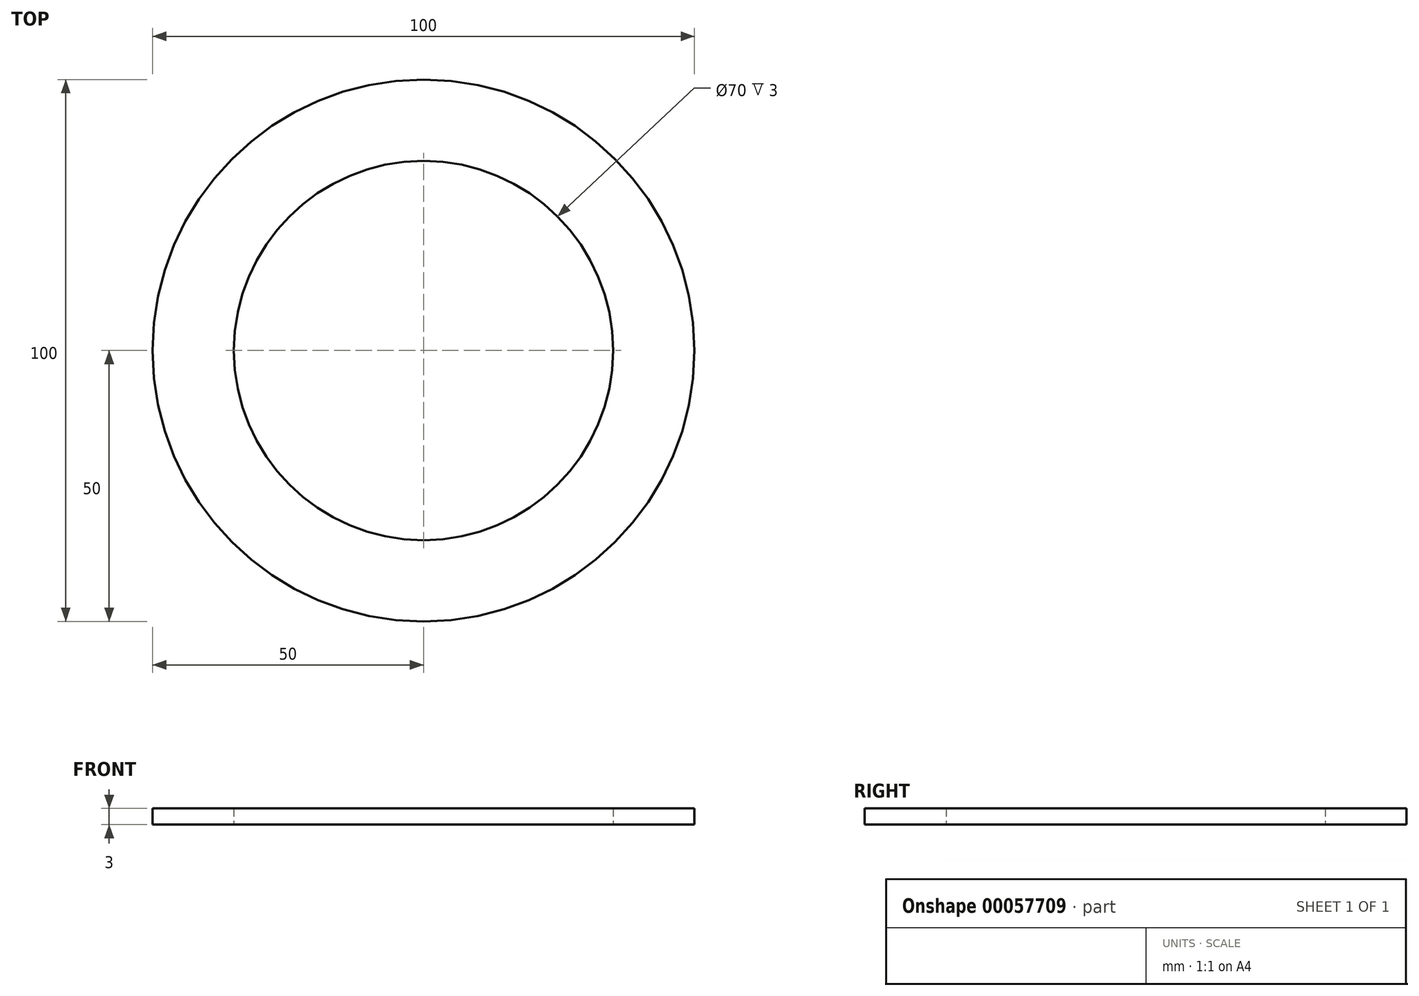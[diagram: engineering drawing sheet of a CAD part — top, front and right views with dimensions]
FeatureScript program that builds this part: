
annotation { "Feature Type Name" : "Feature", "Feature Type Description" : "" }
export const myFeature = defineFeature(function(context is Context, id is Id, definition is map)
    precondition{}
    {
        {
            var Q0;
            Q0=qCreatedBy(makeId("Top.planeOp"),FACE);
            var sketch = newSketch(context, id + "F0", { "sketchPlane" : qUnion([Q0])});
            skCircle(sketch, "E0", {"center": v(0, 0) * mm, "radius": 50 * mm});
            skCircle(sketch, "E1.0", {"center": v(0, 0) * mm, "radius": 35 * mm});
            skSolve(sketch);
        }
        {
            var Q0;
            Q0 = qSketchRegion(id + "F0", true);
            extrude(context, id + "F1", {"entities" : qUnion([Q0]), "depth" : 3 * mm});
        }
    });
